# Revit family: NBS_WallgateLtd_WlHngWshBsns_WHB-100
name_source: partatom
category: Plumbing Fixtures
revit_build: Autodesk Revit 2014 (Build: 20130709_2115(x64)
units: mm (PartAtom-declared; Revit-internal decimal feet)

## types (1)
- WHB-100
    AssetType = Fixed
    BIMObjectName = NBS_WallgateLtd_WallHungWashBasins_WHB-100
    Description = Anti-vandal solid surface basin with through wall fixings
    DrainSize = 32 mm
    DurationUnit = year
    Features = Hygienic and easily cleaned, highly vandal-resistant,
    FixingMaterial = NBS_Concept
    IfcExportAs = IfcSanitaryTerminalType
    IfcExportType = WASHHANDBASIN
    IntegralAccessoryOptions = MA - Thames, MAH - Frost, MAW - White, MC - Bluestone, MCA - Aubergine, MCB - Diamantina, MCC - Black, MCD - Orange, MCE - Pink, MO - Slate, MS - Hyco, MCJ - Light Grey, MCF - NHS Blue
    ManufacturerName = Wallgate Ltd
    ManufacturerURL = www.wallgate.com
    Material = High-grade solid surface material
    ModelNumber = WHB-100
    NBSCertification = www.nationalbimlibrary.com/cert/hmagpg0k
    NBSDescription = Wall hung wash basins
    NBSReference = 45-35-70/369
    Name = WallHungWashBasins_WHB-100_WallgateLtd
    NominalDepth = 350 mm
    NominalHeight = 145 mm
    NominalLength = 0 mm  [stored 0 ft]
    NominalWidth = 470 mm
    ProductInformation = www.wallgate.com/products/wash-basins/whb-100-basin-range
    Size = 470 x 350 x 145 mm
    Standard = BS 3402
    SurfaceSpreadOfFlame = Compliant to Grade 5
    Uniclass2 = 45-31-79/494
    Version = 1
    WarrantyDurationParts = 1
    WarrantyDurationUnit = year
    WashBasinMaterial = NBS_Concept
    WashHandBasinMounting = WallHung
    WashHandBasinType = HandRinse
    WaterSupplyOverflowAndWasteHolesOverflow = None
    WaterSupplyOverflowAndWasteHolesWaste = Bottom waste outlet

note: [stored X ft] marks values corroborated as IEEE doubles in the binary element streams (Revit-internal decimal feet)

## geometry (parser evidence)
native form markers: Sweep x1
no freeform markers — native parametric forms only
